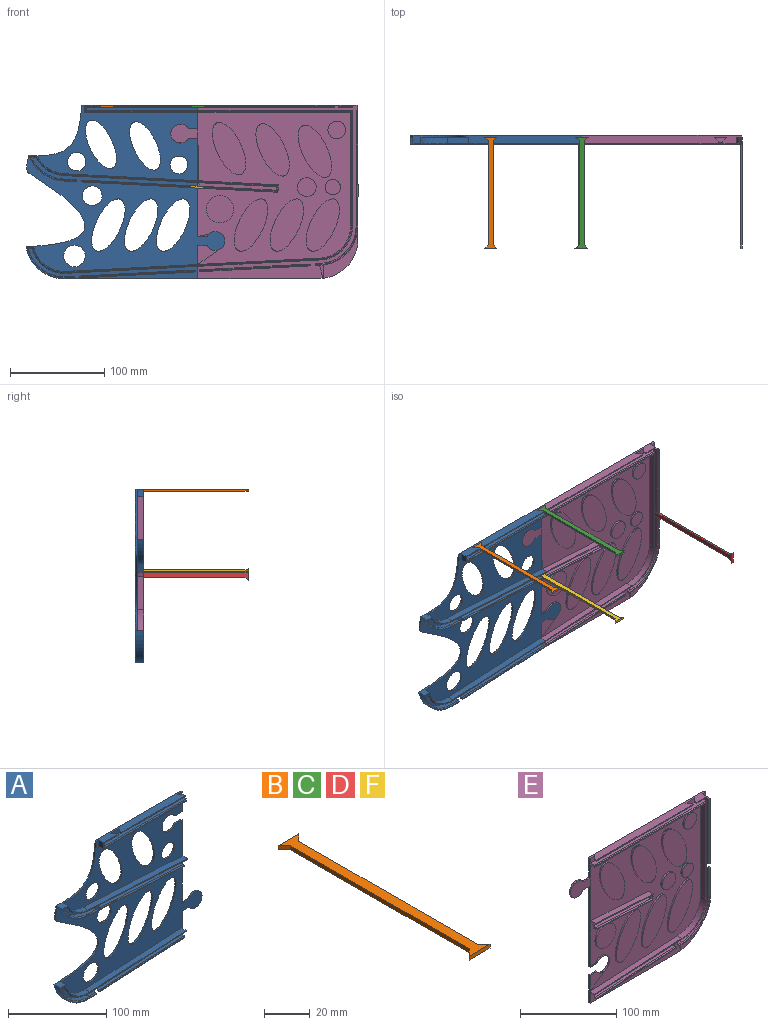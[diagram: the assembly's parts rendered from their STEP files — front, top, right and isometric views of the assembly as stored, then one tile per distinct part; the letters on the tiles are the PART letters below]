
ASSEMBLY  parts=6 mates=5
PART A: 102 faces, bbox 212x9x184.1 mm
  f0: plane 9.04x7mm, normal (0.05,0,-1), area 55.4mm2, adj f19,f34,f53,f98,f99
  f1: plane 122.57x7mm, normal (0.05,0,-1), area 843.2mm2, adj f4,f19,f96,f97,f100,f101
  f2: plane 9.04x6mm, normal (-0.05,0,1), area 46.3mm2, adj f19,f50,f72,f98,f99
  f3: plane 122.57x6.42mm, normal (-0.05,0,1), area 720.4mm2, adj f5,f19,f96,f97,f100,f101
  f4: plane 122.62x7.42mm, normal (0,-1,0), area 122.7mm2, adj f1,f5,f96,f101
  f5: plane 122.62x7.42mm, normal (-0.04,-0.71,0.71), area 173.6mm2, adj f3,f4,f96,f101
  f6: plane 120.45x7mm, normal (-0.05,0,-1), area 828.3mm2, adj f8,f18,f90,f91,f94,f95
  f7: plane 120.45x6.31mm, normal (0.05,0,1), area 707.7mm2, adj f9,f18,f90,f91,f94,f95
  f8: plane 120.5x7.31mm, normal (0,-1,0), area 120.6mm2, adj f6,f9,f90,f95
  f9: plane 120.5x7.31mm, normal (0.04,-0.71,0.71), area 170.6mm2, adj f7,f8,f90,f95
  f10: plane 91.58x6mm, normal (0,0,-1), area 533.5mm2, adj f15,f16,f84,f85,f87,f88
  f11: plane 123x9mm, normal (0,0,1), area 1008.5mm2, adj f12,f13,f16,f17,f28,f29,f45,f66
  f12: plane 119.5x7.75mm, normal (0,-1,0), area 145.8mm2, adj f11,f14,f66,f67,f68,f82,f83,f86
  f13: plane 91.58x1mm, normal (0,-1,0), area 91.6mm2, adj f11,f15,f84,f87
  f14: plane 19.77x1mm, normal (0,-0.71,-0.71), area 27.2mm2, adj f12,f71,f83,f86
  f15: plane 91.58x1mm, normal (0,-0.71,-0.71), area 129.5mm2, adj f10,f13,f84,f87
  f16: plane 118x5.75mm, normal (0,-1,0), area 481.8mm2, adj f10,f11,f28,f69,f70,f71,f85,f88
  f17: plane 170.81x80.04mm, normal (0,-1,0), area 6533.1mm2, adj f11,f24,f25,f26,f27,f28,f29,f35
  f18: plane 211.96x123.1mm, normal (0,-1,0), area 9675.5mm2, adj f6,f7,f20,f21,f22,f23,f24,f31
  f19: plane 179.98x32.11mm, normal (0,-1,0), area 1269.3mm2, adj f0,f1,f2,f3,f20,f43,f46,f50
  f20: plane 35x2mm, normal (1,0,0), area 70mm2, adj f18,f19,f21,f43,f45
  f21: plane 10x2mm, normal (0,0,-1), area 20mm2, adj f18,f20,f22,f45
  f22: cylinder r=10mm len=20mm, axis (0,-1,0), area 104.7mm2, adj f18,f21,f23,f45
  f23: plane 10x2mm, normal (0,0,1), area 20mm2, adj f18,f22,f24,f45
  f24: plane 103.98x2mm, normal (1,0,0), area 208mm2, adj f17,f18,f23,f25,f45,f65
  f25: plane 9.97x2mm, normal (0,0,1), area 19.9mm2, adj f17,f24,f26,f45
  f26: cylinder r=10.05mm len=20.1mm, axis (0,-1,0), area 105.1mm2, adj f17,f25,f27,f45
  f27: plane 9.97x2mm, normal (0,0,-1), area 19.9mm2, adj f17,f26,f28,f45
  f28: plane 24.95x2mm, normal (1,0,0), area 49.9mm2, adj f11,f16,f17,f27,f45
  f29: extruded ~53.45x47.81mm, area 166.5mm2, adj f11,f17,f30,f45
  f30: extruded ~9x8.48mm, area 76.3mm2, adj f29,f31,f45,f55,f56,f64
  f31: extruded ~18.82x2.49mm, area 39.8mm2, adj f18,f30,f32,f45
  f32: extruded ~77.58x59.36mm, area 293.7mm2, adj f18,f31,f33,f45
  f33: extruded ~9x7.82mm, area 70.5mm2, adj f32,f34,f45,f49,f53
  f34: cylinder r=41.25mm len=42.78mm, axis (0,-1,0), area 537.8mm2, adj f0,f33,f43,f45,f53
  f35: extruded ~51.34x32.79mm, area 262mm2, adj f17,f45
  f36: cylinder r=9.49mm len=18.98mm, axis (0,-1,0), area 119.2mm2, adj f17,f45
  f37: cylinder r=9.85mm len=19.71mm, axis (0,-1,0), area 123.8mm2, adj f17,f45
  f38: extruded ~55.47x35.43mm, area 283mm2, adj f18,f45
  f39: extruded ~55.47x35.43mm, area 283mm2, adj f18,f45
  f40: extruded ~55.47x35.43mm, area 283mm2, adj f18,f45
  f41: cylinder r=11.37mm len=22.74mm, axis (0,-1,0), area 142.9mm2, adj f18,f45
  f42: cylinder r=10.45mm len=20.89mm, axis (0,-1,0), area 131.3mm2, adj f18,f45
  f43: plane 139.63x2mm, normal (0,0,-1), area 279.3mm2, adj f19,f20,f34,f45
  f44: extruded ~51.34x32.79mm, area 262mm2, adj f17,f45
  f45: plane 211.96x184.08mm, normal (0,1,0), area 19854.4mm2, adj f11,f20,f21,f22,f23,f24,f25,f26
  f46: plane 139.93x7.33mm, normal (0.05,0,-1), area 840.8mm2, adj f19,f47,f52,f74
  f47: plane 7x1.95mm, normal (0.89,0,0.46), area 14.8mm2, adj f18,f46,f48,f53,f74
  f48: plane 139.04x7.29mm, normal (-0.05,0,1), area 974.6mm2, adj f18,f47,f49,f53
  f49: cylinder r=33.5mm len=34.56mm, axis (0,1,0), area 332.7mm2, adj f18,f33,f48,f53
  f50: cylinder r=39.25mm len=40.24mm, axis (0,1,0), area 327.2mm2, adj f2,f19,f51,f73
  f51: plane 6x3.87mm, normal (0,0,-1), area 23.2mm2, adj f19,f50,f52,f75
  f52: cylinder r=35.5mm len=36.18mm, axis (0,1,0), area 290.6mm2, adj f19,f46,f51,f76
  f53: plane 181.92x34.45mm, normal (0,-1,0), area 262.2mm2, adj f0,f33,f34,f47,f48,f49,f72,f73
  f54: plane 143.28x7.51mm, normal (0.05,0,1), area 1004.3mm2, adj f17,f55,f63,f64,f65
  f55: cylinder r=33.5mm len=28.53mm, axis (0,1,0), area 252.5mm2, adj f17,f30,f54,f64
  f56: cylinder r=41.25mm len=36.6mm, axis (0,1,0), area 337.7mm2, adj f18,f30,f57,f64
  f57: plane 13.6x7mm, normal (-0.05,0,-1), area 87.3mm2, adj f18,f56,f64,f92,f93
  f58: plane 13.6x6mm, normal (0.05,0,1), area 73.7mm2, adj f18,f59,f77,f92,f93
  f59: cylinder r=39.25mm len=33.7mm, axis (0,1,0), area 257.4mm2, adj f18,f58,f60,f79
  f60: plane 6x4.16mm, normal (0,0,-1), area 25mm2, adj f18,f59,f61,f81
  f61: cylinder r=35.5mm len=29.73mm, axis (0,1,0), area 222.5mm2, adj f18,f60,f62,f80
  f62: plane 142.39x7.46mm, normal (-0.05,0,-1), area 855.5mm2, adj f18,f61,f63,f78
  f63: plane 7x1.95mm, normal (0.89,0,-0.46), area 14.8mm2, adj f54,f62,f64,f65,f78
  f64: plane 180.29x27.83mm, normal (0,-1,0), area 247.1mm2, adj f30,f54,f55,f56,f57,f63,f77,f78
  f65: plane 2x1mm, normal (0,1,0), area 1mm2, adj f24,f54,f63
  f66: plane 7.75x7mm, normal (-1,0,0), area 54.3mm2, adj f11,f12,f17,f67
  f67: plane 119x7mm, normal (0,0,-1), area 833mm2, adj f12,f17,f66,f68
  f68: plane 7x2mm, normal (0.89,0,-0.45), area 15.1mm2, adj f12,f17,f67,f69,f82
  f69: plane 118x6mm, normal (0,0,1), area 708mm2, adj f16,f68,f70,f82
  f70: plane 6x3.75mm, normal (1,0,0), area 22.5mm2, adj f16,f69,f71,f83
  f71: plane 18.77x6mm, normal (0,0,-1), area 104.6mm2, adj f14,f16,f70,f86,f89
  f72: plane 9.09x1.47mm, normal (-0.04,-0.71,0.71), area 12.8mm2, adj f2,f53,f73,f98
  f73: cone r=40.25mm half-angle=45deg, axis (0,-1,0), area 79mm2, adj f50,f53,f72,f75
  f74: plane 139.99x8.31mm, normal (0.04,-0.71,-0.71), area 197.9mm2, adj f46,f47,f53,f76
  f75: plane 5.9x1.01mm, normal (0,-0.71,-0.71), area 6.9mm2, adj f51,f53,f73,f76
  f76: cone r=35.5mm half-angle=45deg, axis (0,1,0), area 68.1mm2, adj f52,f53,f74,f75
  f77: plane 13.65x1.71mm, normal (0.04,-0.71,0.71), area 19.3mm2, adj f58,f64,f79,f92
  f78: plane 142.89x8.46mm, normal (-0.04,-0.71,-0.71), area 202mm2, adj f62,f63,f64,f80
  f79: cone r=40.25mm half-angle=45deg, axis (0,-1,0), area 62.5mm2, adj f59,f64,f77,f81
  f80: cone r=35.5mm half-angle=45deg, axis (0,1,0), area 52.1mm2, adj f61,f64,f78,f81
  f81: plane 6.32x1.02mm, normal (0,-0.71,-0.71), area 7.4mm2, adj f60,f64,f79,f80
  f82: plane 119x1mm, normal (0,-0.71,0.71), area 167.2mm2, adj f12,f68,f69,f83
  f83: plane 5.75x1mm, normal (0.71,-0.71,0), area 6.7mm2, adj f12,f14,f70,f82
  f84: plane 3x2mm, normal (1,0,0), area 5.5mm2, adj f10,f11,f13,f15,f85
  f85: plane 4x4mm, normal (0.71,0.71,0), area 11.3mm2, adj f10,f11,f16,f84
  f86: plane 3x2mm, normal (1,0,0), area 5.5mm2, adj f11,f12,f14,f71,f89
  f87: plane 3x2mm, normal (-1,0,0), area 5.5mm2, adj f10,f11,f13,f15,f88
  f88: plane 4x4mm, normal (-0.71,0.71,0), area 11.3mm2, adj f10,f11,f16,f87
  f89: plane 4x4mm, normal (0.71,0.71,0), area 11.3mm2, adj f11,f16,f71,f86
  f90: plane 3x2mm, normal (1,0,-0.05), area 5.5mm2, adj f6,f7,f8,f9,f91
  f91: plane 4.1x4mm, normal (0.71,0.71,-0.04), area 11.3mm2, adj f6,f7,f18,f90
  f92: plane 3x2mm, normal (1,0,-0.05), area 5.5mm2, adj f57,f58,f64,f77,f93
  f93: plane 4.1x4mm, normal (0.71,0.71,-0.04), area 11.3mm2, adj f18,f57,f58,f92
  f94: plane 4.1x4mm, normal (-0.71,0.71,0.04), area 11.3mm2, adj f6,f7,f18,f95
  f95: plane 3x2mm, normal (-1,0,0.05), area 5.5mm2, adj f6,f7,f8,f9,f94
  f96: plane 3x2mm, normal (1,0,0.05), area 5.5mm2, adj f1,f3,f4,f5,f97
  f97: plane 4.1x4mm, normal (0.71,0.71,0.04), area 11.3mm2, adj f1,f3,f19,f96
  f98: plane 3x2mm, normal (1,0,0.05), area 5.5mm2, adj f0,f2,f53,f72,f99
  f99: plane 4.1x4mm, normal (0.71,0.71,0.04), area 11.3mm2, adj f0,f2,f19,f98
  f100: plane 4.1x4mm, normal (-0.71,0.71,-0.04), area 11.3mm2, adj f1,f3,f19,f101
  f101: plane 3x2mm, normal (-1,0,-0.05), area 5.5mm2, adj f1,f3,f4,f5,f100
PART B: 10 faces, bbox 12.9x118x2.1 mm
  f0: plane 3.95x3.95mm, normal (-0.71,0.71,0), area 11.7mm2, adj f1,f7,f8,f9
  f1: plane 12.9x2.1mm, normal (0,-1,0), area 27.1mm2, adj f0,f2,f8,f9
  f2: plane 3.95x3.95mm, normal (0.71,0.71,0), area 11.7mm2, adj f1,f3,f8,f9
  f3: plane 110.1x2.1mm, normal (1,0,0), area 231.2mm2, adj f2,f4,f8,f9
  f4: plane 3.95x3.95mm, normal (0.71,-0.71,0), area 11.7mm2, adj f3,f5,f8,f9
  f5: plane 12.9x2.1mm, normal (0,1,0), area 27.1mm2, adj f4,f6,f8,f9
  f6: plane 3.95x3.95mm, normal (-0.71,-0.71,0), area 11.7mm2, adj f5,f7,f8,f9
  f7: plane 110.1x2.1mm, normal (-1,0,0), area 231.2mm2, adj f0,f6,f8,f9
  f8: plane 118x12.9mm, normal (0,0,1), area 621.2mm2, adj f0,f1,f2,f3,f4,f5,f6,f7
  f9: plane 118x12.9mm, normal (0,0,-1), area 621.2mm2, adj f0,f1,f2,f3,f4,f5,f6,f7
PART C: same geometry as B
PART D: same geometry as B
PART E: 98 faces, bbox 198.7x9x184 mm
  f0: plane 82.39x6mm, normal (-1,0,0), area 486.3mm2, adj f3,f46,f48,f96,f97
  f1: plane 82.39x1mm, normal (0,-1,0), area 82.4mm2, adj f2,f3,f48,f97
  f2: plane 141.03x9mm, normal (1,0,0), area 1086.1mm2, adj f1,f9,f29,f30,f45,f46,f47,f48
  f3: plane 82.39x1mm, normal (-0.71,-0.71,0), area 116.5mm2, adj f0,f1,f48,f97
  f4: plane 117.42x7mm, normal (0.05,0,-1), area 807mm2, adj f10,f46,f87,f88,f91,f92
  f5: plane 6.33x3.33mm, normal (0.05,0,-1), area 15.5mm2, adj f9,f47,f89,f93
  f6: plane 5.38x3.38mm, normal (-0.05,0,1), area 12.5mm2, adj f8,f12,f89,f93
  f7: plane 117.42x6.15mm, normal (-0.05,0,1), area 689.5mm2, adj f11,f46,f87,f88,f91,f92
  f8: cylinder r=40mm len=40.05mm, axis (0,1,0), area 377.1mm2, adj f6,f46,f49,f75,f89
  f9: plane 76.94x45.38mm, normal (0,-1,0), area 103.3mm2, adj f2,f5,f12,f47,f74,f75,f93,f94
  f10: plane 117.47x7.15mm, normal (0,-1,0), area 117.6mm2, adj f4,f11,f87,f91
  f11: plane 117.47x7.15mm, normal (-0.04,-0.71,0.71), area 166.3mm2, adj f7,f10,f87,f91
  f12: plane 3.4x1.18mm, normal (-0.04,-0.71,0.71), area 4.8mm2, adj f6,f9,f75,f93
  f13: plane 83.45x7mm, normal (-0.05,0,-1), area 577mm2, adj f15,f21,f50,f85,f86
  f14: plane 81.46x6mm, normal (0.05,0,1), area 481.4mm2, adj f16,f21,f54,f85,f86
  f15: plane 84.91x12.16mm, normal (0,-1,0), area 174.1mm2, adj f13,f16,f50,f51,f52,f76,f77,f86
  f16: plane 82.46x5.32mm, normal (0.04,-0.71,0.71), area 116.1mm2, adj f14,f15,f77,f86
  f17: plane 142.1x6mm, normal (0,0,-1), area 836.6mm2, adj f20,f46,f81,f82,f83,f84
  f18: plane 14.5x6mm, normal (0,0,-1), area 79mm2, adj f46,f55,f78,f79,f80
  f19: plane 142.1x1mm, normal (0,-1,0), area 142.1mm2, adj f20,f31,f82,f83
  f20: plane 142.1x1mm, normal (0,-0.71,-0.71), area 201mm2, adj f17,f19,f82,f83
  f21: plane 190.91x161.2mm, normal (0,-1,0), area 15925mm2, adj f13,f14,f22,f23,f24,f25,f26,f27
  f22: plane 10x2mm, normal (0,0,-1), area 20mm2, adj f21,f23,f43,f45
  f23: plane 103.98x2mm, normal (-1,0,0), area 208mm2, adj f21,f22,f24,f45
  f24: plane 9.97x2mm, normal (0,0,-1), area 19.9mm2, adj f21,f23,f25,f45
  f25: cylinder r=10.05mm len=20.1mm, axis (0,-1,0), area 105.1mm2, adj f21,f24,f26,f45
  f26: plane 9.97x2mm, normal (0,0,1), area 19.9mm2, adj f21,f25,f27,f45
  f27: plane 34.95x2mm, normal (-1,0,0), area 69.9mm2, adj f21,f26,f28,f45,f46,f58
  f28: plane 128x2mm, normal (0,0,-1), area 256mm2, adj f27,f29,f45,f46
  f29: cylinder r=42mm len=42mm, axis (0,-1,0), area 131.9mm2, adj f2,f28,f45,f46
  f30: cylinder r=1mm len=2mm, axis (0,-1,0), area 3.1mm2, adj f2,f31,f45,f46
  f31: plane 169x9mm, normal (0,0,1), area 1410.2mm2, adj f19,f30,f32,f45,f46,f55,f56,f79
  f32: plane 25x2mm, normal (-1,0,0), area 50mm2, adj f21,f31,f33,f45,f46,f57
  f33: plane 10x2mm, normal (0,0,1), area 20mm2, adj f21,f32,f43,f45
  f34: cylinder r=8.23mm len=16.45mm, axis (0,-1,0), area 103.4mm2, adj f21,f45
  f35: cylinder r=14.51mm len=29.02mm, axis (0,-1,0), area 182.4mm2, adj f21,f45
  f36: cylinder r=10mm len=20mm, axis (0,-1,0), area 125.7mm2, adj f21,f45
  f37: extruded ~55.47x35.43mm, area 283mm2, adj f21,f45
  f38: extruded ~55.47x35.43mm, area 283mm2, adj f21,f45
  f39: extruded ~55.47x35.43mm, area 283mm2, adj f21,f45
  f40: extruded ~55.47x35.43mm, area 283mm2, adj f21,f45
  f41: extruded ~55.47x35.43mm, area 283mm2, adj f21,f45
  f42: extruded ~55.47x35.43mm, area 283mm2, adj f21,f45
  f43: cylinder r=10mm len=20mm, axis (0,-1,0), area 104.7mm2, adj f21,f22,f33,f45
  f44: cylinder r=9.35mm len=18.7mm, axis (0,-1,0), area 117.5mm2, adj f21,f45
  f45: plane 198.66x184.03mm, normal (0,1,0), area 21923.3mm2, adj f2,f22,f23,f24,f25,f26,f27,f28
  f46: plane 184.03x170mm, normal (0,-1,0), area 3871.5mm2, adj f0,f2,f4,f7,f8,f17,f18,f27
  f47: cylinder r=42mm len=42mm, axis (0,1,0), area 461.8mm2, adj f2,f5,f9,f46,f90
  f48: plane 7x2mm, normal (0,0,1), area 13.5mm2, adj f0,f1,f2,f3,f46
  f49: plane 34.76x6mm, normal (-1,0,0), area 200.6mm2, adj f8,f46,f74,f94,f95
  f50: plane 7.74x7mm, normal (1,0,-0.05), area 54.3mm2, adj f13,f15,f21,f51
  f51: plane 84.41x7mm, normal (0.05,0,1), area 591.7mm2, adj f15,f21,f50,f52
  f52: plane 7x1.95mm, normal (-0.89,0,0.46), area 14.8mm2, adj f15,f21,f51,f53,f76
  f53: plane 83.3x6mm, normal (-0.05,0,-1), area 500.5mm2, adj f21,f52,f54,f76
  f54: plane 6x3.75mm, normal (-1,0,0.05), area 22.5mm2, adj f14,f21,f53,f77
  f55: plane 7x2mm, normal (1,0,0), area 13.5mm2, adj f18,f31,f46,f56,f78
  f56: plane 14.5x1mm, normal (0,-1,0), area 14.5mm2, adj f31,f55,f78,f79
  f57: plane 2x1mm, normal (0,1,0), area 1mm2, adj f32,f60,f61
  f58: plane 2x1mm, normal (0,1,0), area 1mm2, adj f27,f64,f65
  f59: plane 164.25x6mm, normal (0,0,1), area 985.5mm2, adj f46,f60,f68,f70
  f60: plane 7x2mm, normal (-0.89,0,0.45), area 15.1mm2, adj f57,f59,f61,f69,f70
  f61: plane 163.25x7mm, normal (0,0,-1), area 1142.8mm2, adj f21,f57,f60,f62,f69
  f62: plane 120.25x7mm, normal (-1,0,0), area 841.8mm2, adj f21,f61,f63,f69
  f63: cylinder r=34.25mm len=34.44mm, axis (0,1,0), area 377.9mm2, adj f21,f62,f64,f69
  f64: plane 128.81x7mm, normal (-0.05,0,1), area 902.9mm2, adj f21,f58,f63,f65,f69
  f65: plane 7x1.95mm, normal (-0.89,0,-0.46), area 14.8mm2, adj f58,f64,f66,f69,f73
  f66: plane 127.86x6.7mm, normal (0.05,0,-1), area 768.2mm2, adj f46,f65,f67,f73
  f67: cylinder r=36.25mm len=36.4mm, axis (0,1,0), area 342.5mm2, adj f46,f66,f68,f72
  f68: plane 122.25x6mm, normal (1,0,0), area 733.5mm2, adj f46,f59,f67,f71
  f69: plane 164.25x163.23mm, normal (0,-1,0), area 467.8mm2, adj f60,f61,f62,f63,f64,f65,f70,f71
  f70: plane 164.75x1mm, normal (0,-0.71,0.71), area 231.9mm2, adj f59,f60,f69,f71
  f71: plane 122.25x1mm, normal (0.71,-0.71,0), area 172.2mm2, adj f68,f69,f70,f72
  f72: cone r=36.25mm half-angle=45deg, axis (0,1,0), area 79.6mm2, adj f67,f69,f71,f73
  f73: plane 128.36x7.7mm, normal (0.04,-0.71,-0.71), area 181.4mm2, adj f65,f66,f69,f72
  f74: plane 34.76x1mm, normal (-0.71,-0.71,0), area 49.2mm2, adj f9,f49,f75,f94
  f75: cone r=41mm half-angle=45deg, axis (0,-1,0), area 90mm2, adj f8,f9,f12,f74
  f76: plane 84.35x5.34mm, normal (-0.04,-0.71,-0.71), area 118.4mm2, adj f15,f52,f53,f77
  f77: plane 5.74x1.25mm, normal (-0.71,-0.71,0.04), area 6.7mm2, adj f15,f16,f54,f76
  f78: plane 14.5x1mm, normal (0,-0.71,-0.71), area 20.5mm2, adj f18,f55,f56,f79
  f79: plane 3x2mm, normal (-1,0,0), area 5.5mm2, adj f18,f31,f56,f78,f80
  f80: plane 4x4mm, normal (-0.71,0.71,0), area 11.3mm2, adj f18,f31,f46,f79
  f81: plane 4x4mm, normal (0.71,0.71,0), area 11.3mm2, adj f17,f31,f46,f82
  f82: plane 3x2mm, normal (1,0,0), area 5.5mm2, adj f17,f19,f20,f31,f81
  f83: plane 3x2mm, normal (-1,0,0), area 5.5mm2, adj f17,f19,f20,f31,f84
  f84: plane 4x4mm, normal (-0.71,0.71,0), area 11.3mm2, adj f17,f31,f46,f83
  f85: plane 4.1x4mm, normal (-0.71,0.71,0.04), area 11.3mm2, adj f13,f14,f21,f86
  f86: plane 3x2mm, normal (-1,0,0.05), area 5.5mm2, adj f13,f14,f15,f16,f85
  f87: plane 3x2mm, normal (-1,0,-0.05), area 5.5mm2, adj f4,f7,f10,f11,f88
  f88: plane 4.1x4mm, normal (-0.71,0.71,-0.04), area 11.3mm2, adj f4,f7,f46,f87
  f89: plane 4.1x4mm, normal (-0.71,0.71,-0.04), area 11.3mm2, adj f5,f6,f8,f46,f90,f93
  f90: plane 0.67x0.67mm, normal (-0.05,0,1), area 0.2mm2, adj f46,f47,f89
  f91: plane 3x2mm, normal (1,0,0.05), area 5.5mm2, adj f4,f7,f10,f11,f92
  f92: plane 4.1x4mm, normal (0.71,0.71,0.04), area 11.3mm2, adj f4,f7,f46,f91
  f93: plane 3x2mm, normal (-1,0,-0.05), area 5.5mm2, adj f5,f6,f9,f12,f89
  f94: plane 3x2mm, normal (0,0,1), area 5.5mm2, adj f2,f9,f49,f74,f95
  f95: plane 4x4mm, normal (0,0.71,0.71), area 11.3mm2, adj f2,f46,f49,f94
  f96: plane 4x4mm, normal (0,0.71,-0.71), area 11.3mm2, adj f0,f2,f46,f97
  f97: plane 3x2mm, normal (0,0,-1), area 5.5mm2, adj f0,f1,f2,f3,f96
PART F: same geometry as B
PLACE A at identity
PLACE B t=(-81.88,227.51,181.93)mm
PLACE C t=(14.8,227.51,181.93)mm
PLACE D rot(axis=(0,-1,0),90deg) t=(309.63,227.51,-31.49)mm
PLACE E at identity fixed
PLACE F rot(axis=(0,-1,0),177deg) t=(263.4,227.46,91.75)mm
MATE fastened A.f28 <-> E.f32  axis (1,0,0) through (139.63,0,184.03)mm
MATE fastened E.f46 <-> C.f5  axis (0,-1,0) through (139.63,0,184.03)mm
MATE fastened E.f46 <-> D.f5  axis (0,-1,0) through (309.63,0,93.34)mm
MATE fastened F.f9 <-> A.f7  axis (0.05,0,1) through (136.24,-4,98.41)mm
MATE fastened A.f16 <-> B.f5  axis (0,-1,0) through (42.95,0,184.03)mm
